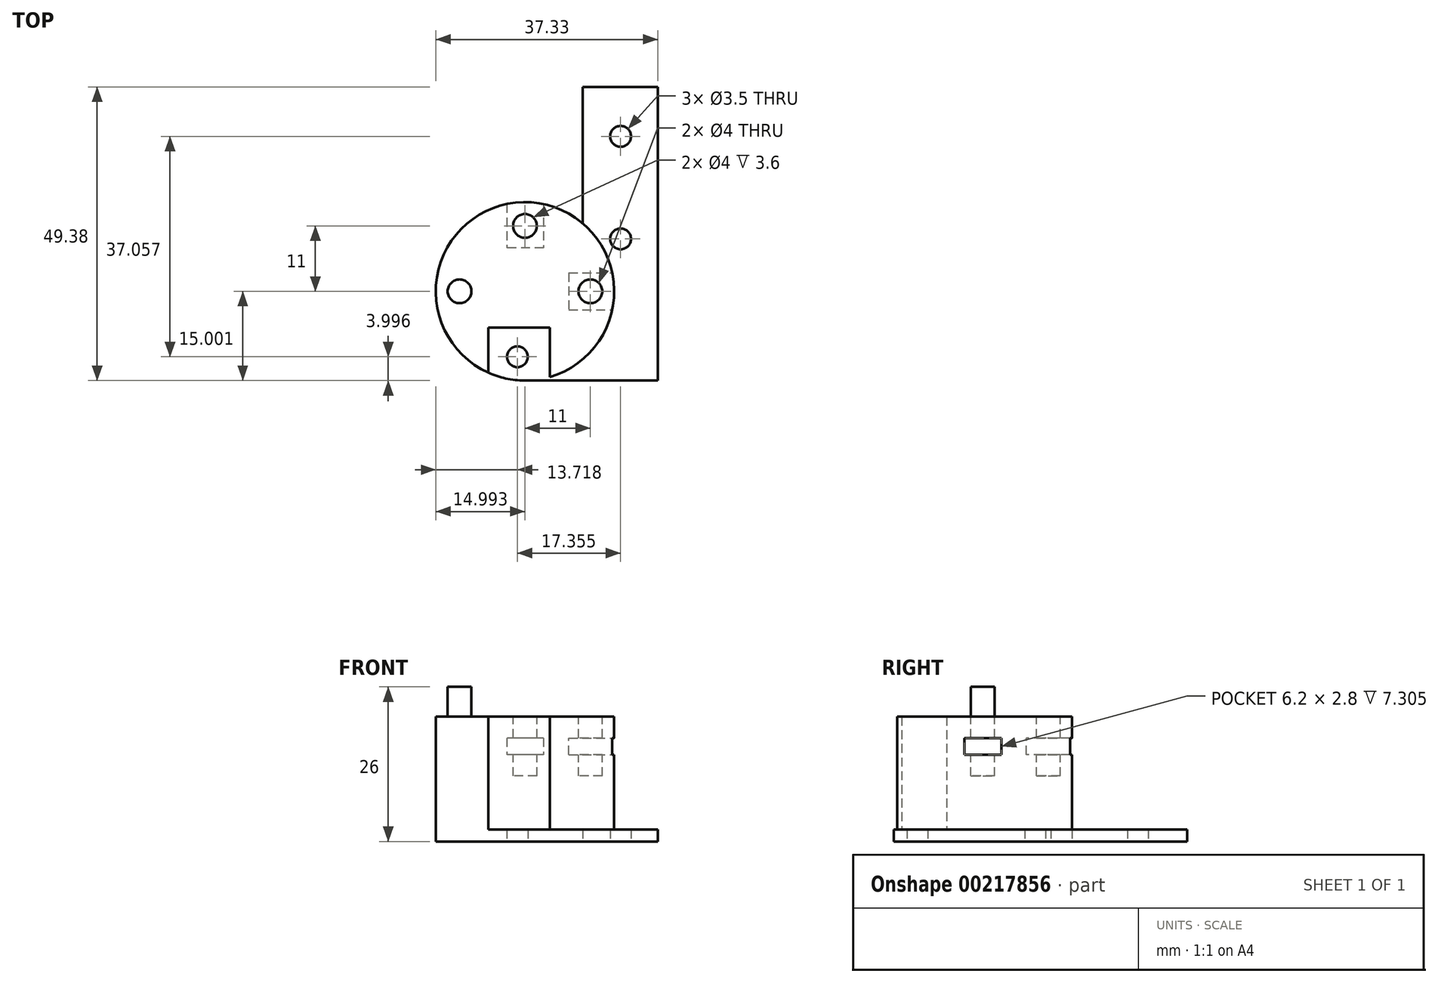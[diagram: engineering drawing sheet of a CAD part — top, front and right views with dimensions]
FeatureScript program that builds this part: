
annotation { "Feature Type Name" : "Feature", "Feature Type Description" : "" }
export const myFeature = defineFeature(function(context is Context, id is Id, definition is map)
    precondition{}
    {
        {
            var Q0;
            Q0=qCreatedBy(makeId("Top.planeOp"),FACE);
            var sketch = newSketch(context, id + "F0", { "sketchPlane" : qUnion([Q0])});
            skCircle(sketch, "E0", {"center": v(14.32, -35.28) * mm, "radius": 1.75 * mm});
            skLineSegment(sketch, "E1", {"start": v(42.26, -9.57) * mm, "end": v(42.26, -9.57) * mm});
            skCircle(sketch, "E2.1.0.0", {"center": v(15.6, 32.82) * mm, "radius": 1.5 * mm});
            skCircle(sketch, "E3", {"center": v(31.67, -15.47) * mm, "radius": 1.75 * mm});
            skCircle(sketch, "E4", {"center": v(31.67, 1.77) * mm, "radius": 1.75 * mm});
            skLineSegment(sketch, "E5.top", {"start": v(25.32, 10.1) * mm, "end": v(37.93, 10.1) * mm});
            skLineSegment(sketch, "E5.right", {"start": v(37.92, -39.28) * mm, "end": v(37.93, 10.1) * mm});
            skLineSegment(sketch, "E6.top", {"start": v(19.77, -30.37) * mm, "end": v(9.42, -30.37) * mm});
            skLineSegment(sketch, "E6.right", {"start": v(9.42, -37.95) * mm, "end": v(9.42, -30.37) * mm});
            skLineSegment(sketch, "E7", {"start": v(19.77, -30.37) * mm, "end": v(25.32, -23.26) * mm});
            skLineSegment(sketch, "E8.trimOffspring", {"start": v(25.32, -23.26) * mm, "end": v(25.32, 10.1) * mm});
            skCircle(sketch, "E9", {"center": v(15.6, -24.28) * mm, "radius": 15 * mm});
            skLineSegment(sketch, "E10", {"start": v(9.42, -30.37) * mm, "end": v(1.89, -30.37) * mm});
            skLineSegment(sketch, "E11", {"start": v(19.77, -30.37) * mm, "end": v(19.77, -38.7) * mm});
            skLineSegment(sketch, "E12", {"start": v(15.47, -39.28) * mm, "end": v(37.92, -39.28) * mm});
            skSolve(sketch);
        }
        {
            var Q0;
            Q0=makeQuery(id+"F0.imprint","IMPRINT",FACE,{"disambiguationData":[TD([[makeQuery(id+"F0.imprint","IMPRINT",EDGE,{"derivedFrom":sQuery(id+"F0.wireOp",EDGE,"E0")}),-1.0]])]});
            var Q1;
            Q1=makeQuery(id+"F0.imprint","IMPRINT",FACE,{"disambiguationData":[TD([[makeQuery(id+"F0.imprint","IMPRINT",EDGE,{"derivedFrom":sQuery(id+"F0.wireOp",EDGE,"E3")}),-1.0]])]});
            var Q2;
            Q2=makeQuery(id+"F0.imprint","IMPRINT",FACE,{"disambiguationData":[TD([[makeQuery(id+"F0.imprint","IMPRINT",EDGE,{"derivedFrom":sQuery(id+"F0.wireOp",EDGE,"E6.top")}),-1.0]])]});
            var Q3;
            {var subQ0=sQuery(id+"F0.wireOp",EDGE,"E7");Q3=makeQuery(id+"F0.imprint","IMPRINT",FACE,{"disambiguationData":[TD([[makeQuery(id+"F0.imprint","IMPRINT",EDGE,{"derivedFrom":subQ0}),-1.0]])]});}
            var Q4;
            {var subQ0=sQuery(id+"F0.wireOp",EDGE,"E10");Q4=makeQuery(id+"F0.imprint","IMPRINT",FACE,{"disambiguationData":[TD([[makeQuery(id+"F0.imprint","IMPRINT",EDGE,{"derivedFrom":subQ0}),1.0]])]});}
            extrude(context, id + "F1", {"entities" : qUnion([Q0, Q1, Q2, Q3, Q4]), "depth" : 2 * mm});
        }
        {
            var Q0;
            Q0=makeQuery(id+"F0.imprint","IMPRINT",FACE,{"disambiguationData":[TD([[makeQuery(id+"F0.imprint","IMPRINT",EDGE,{"derivedFrom":sQuery(id+"F0.wireOp",EDGE,"E6.top")}),-1.0]])]});
            var Q1;
            {var subQ0=sQuery(id+"F0.wireOp",EDGE,"E7");Q1=makeQuery(id+"F0.imprint","IMPRINT",FACE,{"disambiguationData":[TD([[makeQuery(id+"F0.imprint","IMPRINT",EDGE,{"derivedFrom":subQ0}),-1.0]])]});}
            var Q2;
            {var subQ0=sQuery(id+"F0.wireOp",EDGE,"E10");Q2=makeQuery(id+"F0.imprint","IMPRINT",FACE,{"disambiguationData":[TD([[makeQuery(id+"F0.imprint","IMPRINT",EDGE,{"derivedFrom":subQ0}),1.0]])]});}
            extrude(context, id + "F2", {"entities" : qUnion([Q0, Q1, Q2]), "operationType" : NewBodyOperationType.ADD, "depth" : 21 * mm});
        }
        {
            var Q0;
            Q0=makeQuery(id+"F2.opExtrude","CAP_FACE",FACE,{"disambiguationData":[OSD([sQuery(id+"F0.wireOp",EDGE,"E6.top"),sQuery(id+"F0.wireOp",EDGE,"E6.right"),sQuery(id+"F0.wireOp",EDGE,"E9"),sQuery(id+"F0.wireOp",EDGE,"E11")])],"isStart":false});
            var sketch = newSketch(context, id + "F3", { "sketchPlane" : qUnion([Q0])});
            skCircle(sketch, "E13", {"center": v(15.6, -35.28) * mm, "radius": 2 * mm});
            skCircle(sketch, "E14", {"center": v(15.6, -13.28) * mm, "radius": 2 * mm});
            skLineSegment(sketch, "E15", {"start": v(15.6, -35.28) * mm, "end": v(15.6, -13.28) * mm, "construction": true});
            skLineSegment(sketch, "E16", {"start": v(15.6, -24.28) * mm, "end": v(3.75, -24.28) * mm, "construction": true});
            skCircle(sketch, "E17", {"center": v(4.6, -24.28) * mm, "radius": 2 * mm});
            skLineSegment(sketch, "E18", {"start": v(15.6, -24.28) * mm, "end": v(27.6, -24.28) * mm, "construction": true});
            skCircle(sketch, "E19", {"center": v(26.6, -24.28) * mm, "radius": 2 * mm});
            skCircle(sketch, "E20", {"center": v(15.6, -24.28) * mm, "radius": 15 * mm});
            skLineSegment(sketch, "E21", {"start": v(27.6, -24.28) * mm, "end": v(30.6, -24.28) * mm, "construction": true});
            skSolve(sketch);
        }
        {
            var Q0;
            Q0=makeQuery(id+"F3.imprint","IMPRINT",FACE,{"disambiguationData":[TD([[makeQuery(id+"F3.imprint","IMPRINT",EDGE,{"derivedFrom":sQuery(id+"F3.wireOp",EDGE,"E14")}),1.0]])]});
            var Q1;
            Q1=makeQuery(id+"F3.imprint","IMPRINT",FACE,{"disambiguationData":[TD([[makeQuery(id+"F3.imprint","IMPRINT",EDGE,{"derivedFrom":sQuery(id+"F3.wireOp",EDGE,"E19")}),1.0]])]});
            extrude(context, id + "F4", {"entities" : qUnion([Q0, Q1]), "operationType" : NewBodyOperationType.REMOVE, "oppositeDirection" : true, "depth" : 10 * mm});
        }
        {
            var Q0;
            Q0=makeQuery(id+"F2.opExtrude","SWEPT_FACE",FACE,{"disambiguationData":[OSD([sQuery(id+"F0.wireOp",EDGE,"E6.top")])]});
            var sketch = newSketch(context, id + "F5", { "sketchPlane" : qUnion([Q0])});
            skLineSegment(sketch, "E22.bottom", {"start": v(18.72, 14.6) * mm, "end": v(12.52, 14.6) * mm});
            skLineSegment(sketch, "E22.top", {"start": v(18.72, 17.4) * mm, "end": v(12.52, 17.4) * mm});
            skLineSegment(sketch, "E22.left", {"start": v(18.72, 14.6) * mm, "end": v(18.72, 17.4) * mm});
            skLineSegment(sketch, "E22.right", {"start": v(12.52, 14.6) * mm, "end": v(12.52, 17.4) * mm});
            skPoint(sketch, "E22.middle", {"position": v(15.62, 16) * mm});
            skPoint(sketch, "E22.middle.positionSnap0", {"position": v(14.6, 21) * mm});
            skPoint(sketch, "E22.centerSnap0", {"position": v(14.6, 21) * mm});
            skSolve(sketch);
        }
        {
            var Q0;
            Q0=makeQuery(id+"F5.imprint","IMPRINT",FACE,{"disambiguationData":[TD([[makeQuery(id+"F5.imprint","IMPRINT",EDGE,{"derivedFrom":sQuery(id+"F5.wireOp",EDGE,"E22.bottom")}),-1.0]])]});
            extrude(context, id + "F6", {"entities" : qUnion([Q0]), "operationType" : NewBodyOperationType.REMOVE, "oppositeDirection" : true, "depth" : 25 * mm, "hasSecondDirection" : true, "secondDirectionOppositeDirection" : true, "secondDirectionDepth" : 13.4 * mm});
        }
        {
            var Q0;
            Q0=sQuery(id+"F3.wireOp",VERTEX,"E21.end");
            var Q1;
            Q1=sQuery(id+"F3.wireOp",EDGE,"E21");
            cPlane(context, id + "F7", {"entities" : qUnion([Q0, Q1]), "cplaneType" : CPlaneType.LINE_POINT, "offset" : 25 * mm, "width" : 150 * mm, "height" : 150 * mm});
        }
        {
            var Q0;
            Q0=qCreatedBy(id+"F7.planeOp",FACE);
            var sketch = newSketch(context, id + "F8", { "sketchPlane" : qUnion([Q0])});
            skLineSegment(sketch, "E23.bottom", {"start": v(-21.18, 14.6) * mm, "end": v(-27.38, 14.6) * mm});
            skLineSegment(sketch, "E23.top", {"start": v(-21.18, 17.4) * mm, "end": v(-27.38, 17.4) * mm});
            skLineSegment(sketch, "E23.left", {"start": v(-21.18, 14.6) * mm, "end": v(-21.18, 17.4) * mm});
            skLineSegment(sketch, "E23.right", {"start": v(-27.38, 14.6) * mm, "end": v(-27.38, 17.4) * mm});
            skPoint(sketch, "E23.middle", {"position": v(-24.28, 16) * mm});
            skSolve(sketch);
        }
        {
            var Q0;
            Q0=makeQuery(id+"F8.imprint","IMPRINT",FACE,{"disambiguationData":[TD([[makeQuery(id+"F8.imprint","IMPRINT",EDGE,{"derivedFrom":sQuery(id+"F8.wireOp",EDGE,"E23.bottom")}),-1.0]])]});
            extrude(context, id + "F9", {"entities" : qUnion([Q0]), "operationType" : NewBodyOperationType.REMOVE, "oppositeDirection" : true, "depth" : 7.63 * mm});
        }
        {
            var Q0;
            Q0=makeQuery(id+"F3.imprint","IMPRINT",FACE,{"disambiguationData":[TD([[makeQuery(id+"F3.imprint","IMPRINT",EDGE,{"derivedFrom":sQuery(id+"F3.wireOp",EDGE,"E17")}),1.0]])]});
            extrude(context, id + "F10", {"entities" : qUnion([Q0]), "operationType" : NewBodyOperationType.ADD, "depth" : 5 * mm});
        }
    });
